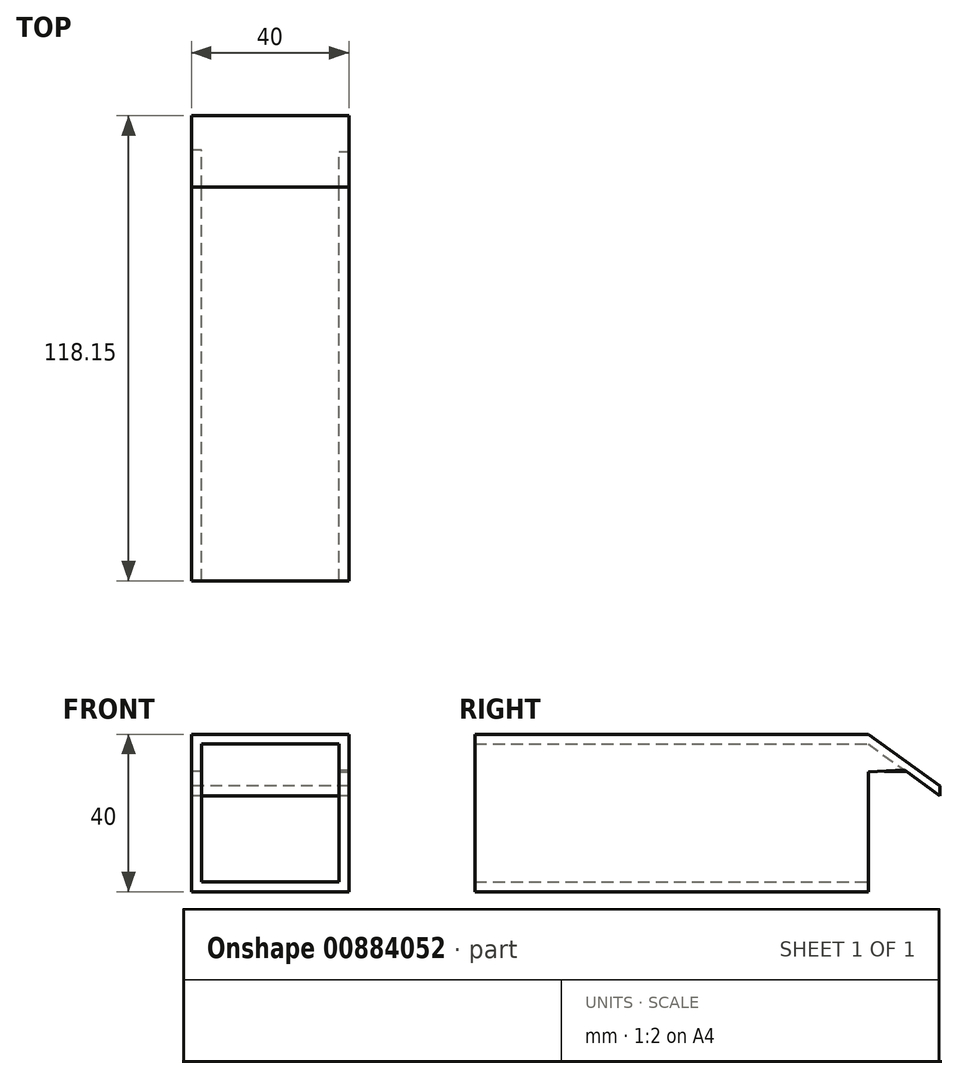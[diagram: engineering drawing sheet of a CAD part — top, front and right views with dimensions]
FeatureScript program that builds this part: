
annotation { "Feature Type Name" : "Feature", "Feature Type Description" : "" }
export const myFeature = defineFeature(function(context is Context, id is Id, definition is map)
    precondition{}
    {
        {
            var Q0;
            Q0=qCreatedBy(makeId("Front.planeOp"),FACE);
            var sketch = newSketch(context, id + "F0", { "sketchPlane" : qUnion([Q0])});
            skLineSegment(sketch, "E0", {"start": v(-64.5, -37.5) * mm, "end": v(-24.5, -37.5) * mm});
            skLineSegment(sketch, "E1", {"start": v(-24.5, 2.5) * mm, "end": v(-24.5, -37.5) * mm});
            skLineSegment(sketch, "E2", {"start": v(-24.5, 2.5) * mm, "end": v(-64.5, 2.5) * mm});
            skLineSegment(sketch, "E3", {"start": v(-64.5, 2.5) * mm, "end": v(-64.5, -37.5) * mm});
            skPoint(sketch, "E4.end.orphan", {"position": v(-62, 2.5) * mm});
            skPoint(sketch, "E5.end.orphan", {"position": v(-64.5, 0) * mm});
            skLineSegment(sketch, "E6", {"start": v(-62, 0) * mm, "end": v(-62, -35) * mm});
            skPoint(sketch, "E7.end.orphan", {"position": v(33, -35) * mm});
            skPoint(sketch, "E7.start.orphan", {"position": v(33, 0) * mm});
            skLineSegment(sketch, "E8", {"start": v(-62, -35) * mm, "end": v(-27, -35) * mm});
            skLineSegment(sketch, "E9", {"start": v(-27, -35) * mm, "end": v(-27, 0) * mm});
            skLineSegment(sketch, "E10", {"start": v(-27, 0) * mm, "end": v(-62, 0) * mm});
            skSolve(sketch);
        }
        {
            var Q0;
            Q0=makeQuery(id+"F0.imprint","IMPRINT",FACE,{"disambiguationData":[TD([[makeQuery(id+"F0.imprint","IMPRINT",EDGE,{"derivedFrom":sQuery(id+"F0.wireOp",EDGE,"E0")}),1.0]])]});
            extrude(context, id + "F1", {"entities" : qUnion([Q0]), "depth" : 100 * mm, "offsetDistance" : 25 * mm});
        }
        {
            var Q0;
            Q0=makeQuery(id+"F1.opExtrude","SWEPT_FACE",FACE,{"disambiguationData":[OSD([sQuery(id+"F0.wireOp",EDGE,"E3")])]});
            var sketch = newSketch(context, id + "F2", { "sketchPlane" : qUnion([Q0])});
            skLineSegment(sketch, "E11", {"start": v(0, 2.5) * mm, "end": v(-18.15, -10.65) * mm});
            skLineSegment(sketch, "E12", {"start": v(0, 0) * mm, "end": v(-18.15, -13.15) * mm});
            skLineSegment(sketch, "E13", {"start": v(-18.15, -13.15) * mm, "end": v(-18.15, -10.65) * mm});
            skSolve(sketch);
        }
        {
            var Q0;
            {var subQ0=sQuery(id+"F2.wireOp",EDGE,"E11");Q0=makeQuery(id+"F2.imprint","IMPRINT",FACE,{"disambiguationData":[TD([[makeQuery(id+"F2.imprint","IMPRINT",EDGE,{"derivedFrom":subQ0}),1.0]])]});}
            extrude(context, id + "F3", {"entities" : qUnion([Q0]), "operationType" : NewBodyOperationType.ADD, "oppositeDirection" : true, "depth" : 40 * mm, "offsetDistance" : 25 * mm});
        }
        {
            var Q0;
            {var subQ0=sQuery(id+"F0.wireOp",EDGE,"E3");Q0=makeQuery(id+"F3.boolean.opBoolean","MERGE",FACE,{"derivedFrom":[makeQuery(id+"F1.opExtrude","SWEPT_FACE",FACE,{"disambiguationData":[OSD([subQ0])]}),makeQuery(id+"F3.opExtrude","CAP_FACE",FACE,{"disambiguationData":[OSD([subQ0,sQuery(id+"F2.wireOp",EDGE,"E11"),sQuery(id+"F2.wireOp",EDGE,"E12"),sQuery(id+"F2.wireOp",EDGE,"E13")])],"isStart":true})]});}
            var sketch = newSketch(context, id + "F4", { "sketchPlane" : qUnion([Q0])});
            skLineSegment(sketch, "E14", {"start": v(-9.48, -6.87) * mm, "end": v(0, -6.87) * mm});
            skLineSegment(sketch, "E15", {"start": v(0, -6.87) * mm, "end": v(0, 0) * mm});
            skLineSegment(sketch, "E16", {"start": v(0, 0) * mm, "end": v(-9.48, -6.87) * mm});
            skSolve(sketch);
        }
        {
            var Q0;
            Q0=makeQuery(id+"F4.imprint","IMPRINT",FACE,{"disambiguationData":[TD([[makeQuery(id+"F4.imprint","IMPRINT",EDGE,{"derivedFrom":sQuery(id+"F4.wireOp",EDGE,"E14")}),1.0]])]});
            extrude(context, id + "F5", {"entities" : qUnion([Q0]), "operationType" : NewBodyOperationType.ADD, "oppositeDirection" : true, "depth" : 2.5 * mm, "offsetDistance" : 25 * mm});
        }
        {
            var Q0;
            Q0=makeQuery(id+"F3.boolean.opBoolean","MERGE",FACE,{"derivedFrom":[makeQuery(id+"F1.opExtrude","SWEPT_FACE",FACE,{"disambiguationData":[OSD([sQuery(id+"F0.wireOp",EDGE,"E1")])]}),makeQuery(id+"F3.opExtrude","CAP_FACE",FACE,{"disambiguationData":[OSD([sQuery(id+"F0.wireOp",EDGE,"E3"),sQuery(id+"F2.wireOp",EDGE,"E11"),sQuery(id+"F2.wireOp",EDGE,"E12"),sQuery(id+"F2.wireOp",EDGE,"E13")])],"isStart":false})]});
            var sketch = newSketch(context, id + "F6", { "sketchPlane" : qUnion([Q0])});
            skLineSegment(sketch, "E17", {"start": v(0, 0) * mm, "end": v(9.07, -6.57) * mm});
            skLineSegment(sketch, "E18", {"start": v(9.07, -6.57) * mm, "end": v(0, -7.1) * mm});
            skLineSegment(sketch, "E19", {"start": v(0, -7.1) * mm, "end": v(0, 0) * mm});
            skSolve(sketch);
        }
        {
            var Q0;
            Q0=makeQuery(id+"F6.imprint","IMPRINT",FACE,{"disambiguationData":[TD([[makeQuery(id+"F6.imprint","IMPRINT",EDGE,{"derivedFrom":sQuery(id+"F6.wireOp",EDGE,"E17")}),-1.0]])]});
            extrude(context, id + "F7", {"entities" : qUnion([Q0]), "operationType" : NewBodyOperationType.ADD, "oppositeDirection" : true, "depth" : 2.5 * mm, "offsetDistance" : 25 * mm});
        }
    });
